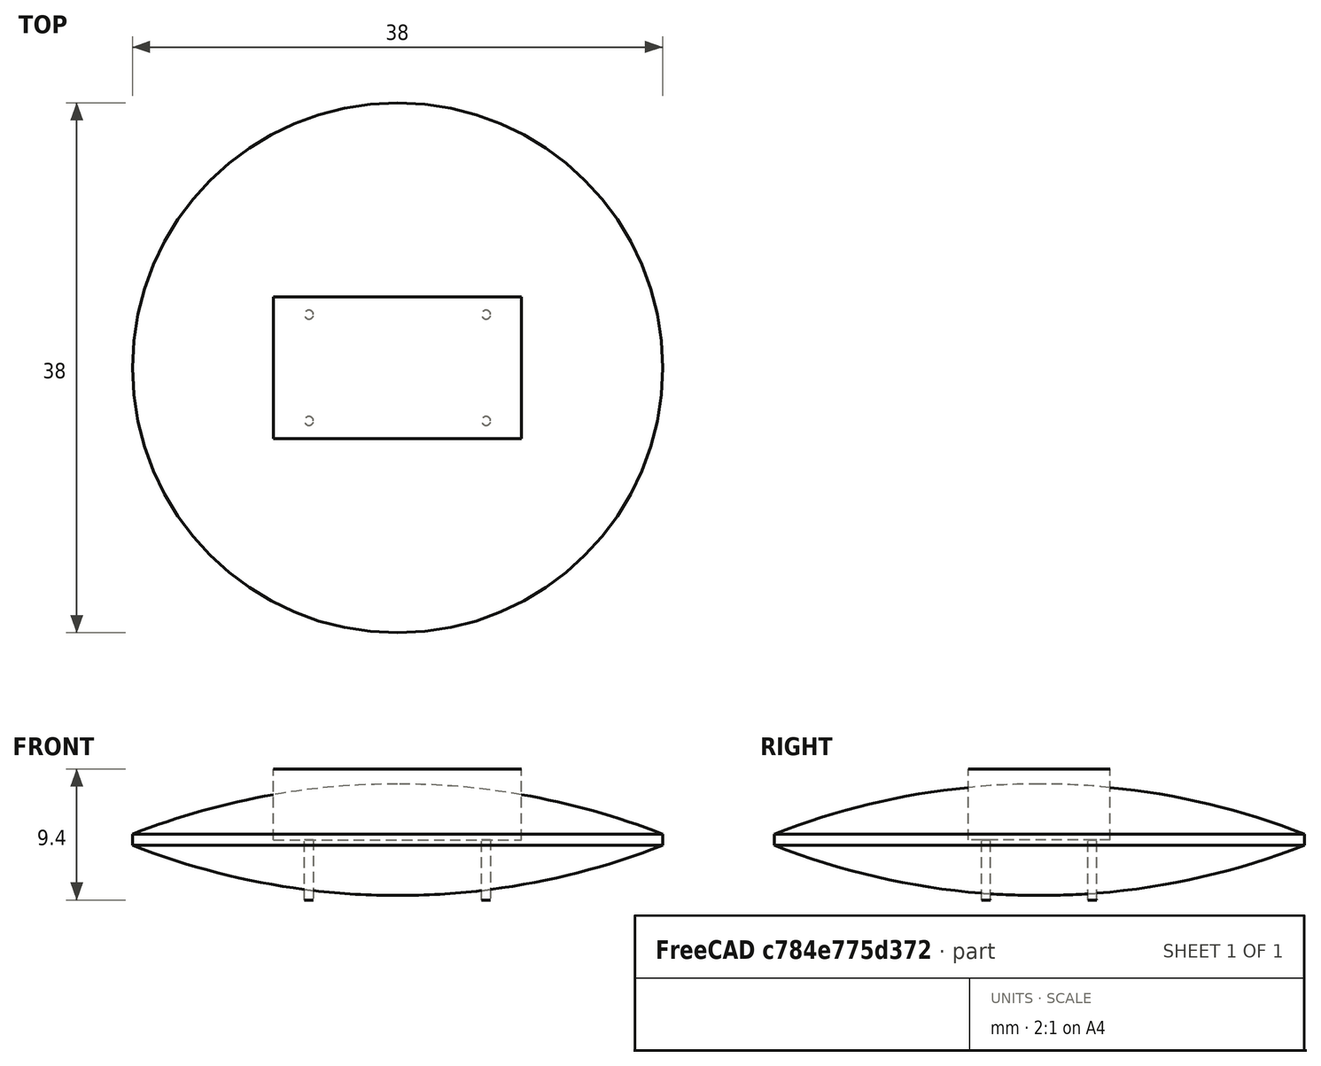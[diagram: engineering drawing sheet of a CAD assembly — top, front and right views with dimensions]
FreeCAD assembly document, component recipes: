
FREECAD ASSEMBLY — COMPONENT RECIPES ("ClockRaytrace")

This assembly document has 4 components, labeled P0..P3 below (a component is one placed body or linked part). 4 of them carry a construction recipe — the FreeCAD feature program that regenerates the part from scratch, quoted from this document or its linked companion documents; the rest are supplied as boundary geometry only. No exploded tour is included for this assembly.
COMPONENT P0 — recipe-attached ("baffle", modeled in this document).
Construction recipe (the document's own serialized feature program — sketch geometry with constraints, then the solid features built on it; lengths are millimeters unless a unit is written):

FEATURE [Sketcher::SketchObject] Sketch011
  ArcFitTolerance = 1e-06
  AttachmentSupport = -> [XY_Plane019]
  FullyConstrained = false
  MakeInternals = false
  MapMode = 5
  sketch-geometry (3):
    g0: Circle CenterX=0 CenterY=0 CenterZ=0 NormalX=0 NormalY=0 NormalZ=1 AngleXU=0 Radius=20
    g1: Circle CenterX=0 CenterY=0 CenterZ=0 NormalX=0 NormalY=0 NormalZ=1 AngleXU=0 Radius=21.5748
    g2: LineSegment [constr] StartX=0.010426 StartY=20 StartZ=0 EndX=0.010426 EndY=21.5748 EndZ=0
  constraints (7):
    c: Coincident(g0,g-1)
    c: Coincident(g1,g0)
    c: Diameter(g0) = 40
    c: PointOnObject(g2,g0)
    c: PointOnObject(g2,g1)
    c: Vertical(g2)
    c: DistanceY(g2,g2) = 1.5748
FEATURE [PartDesign::Pad] Pad006
  Direction = (0,0,1)
  Length = 48
  Length2 = 10
  Profile = -> Sketch011
  ReferenceAxis = -> Sketch011 [N_Axis]
  Refine = true
  Reversed = true
  Suppressed = false
  Type = 0
  expr: Length = Spreadsheet.Base_LensToLED - 3 mm
FEATURE [PartDesign::Body] Body010  label="baffle"
  AllowCompound = false
  Group = -> [Sketch011,Pad006]
  Origin = -> Origin019
  Placement = pos=(-7.46,0,48) rot=(0,-1,0;0.314159rad)
  Tip = -> Pad006
  expr: .Placement.Base.x = 2.54 mm - Spreadsheet.Base_Lens_X_offset
  expr: .Placement.Base.z = Spreadsheet.Base_LensToLED - 3 mm
COMPONENT P1 — recipe-attached ("Wall and Ceiling", modeled in this document).
Construction recipe (the document's own serialized feature program — sketch geometry with constraints, then the solid features built on it; lengths are millimeters unless a unit is written):

FEATURE [Sketcher::SketchObject] Sketch012
  ArcFitTolerance = 1e-06
  AttachmentSupport = -> [XZ_Plane022]
  FullyConstrained = true
  MakeInternals = false
  MapMode = 5
  Placement = pos=(0,0,0) rot=(0,0.707107,0.707107;3.14159rad)
  sketch-geometry (6):
    g0: LineSegment StartX=-76.2 StartY=0 StartZ=0 EndX=-76.2 EndY=1390.42 EndZ=0
    g1: LineSegment StartX=-76.2 StartY=1390.42 StartZ=0 EndX=1751.03 EndY=1390.42 EndZ=0
    g2: LineSegment StartX=1751.03 StartY=1390.42 StartZ=0 EndX=1751.03 EndY=1391.99 EndZ=0
    g3: LineSegment StartX=1751.03 StartY=1391.99 StartZ=0 EndX=-77.7748 EndY=1391.99 EndZ=0
    g4: LineSegment StartX=-77.7748 StartY=1391.99 StartZ=0 EndX=-77.7748 EndY=0 EndZ=0
    g5: LineSegment StartX=-77.7748 StartY=0 StartZ=0 EndX=-76.2 EndY=0 EndZ=0
  constraints (18):
    c: Vertical(g0)
    c: Horizontal(g1)
    c: Coincident(g2,g1)
    c: Vertical(g2)
    c: Horizontal(g3)
    c: PointOnObject(g4,g-1)
    c: Vertical(g4)
    c: Coincident(g5,g0)
    c: DistanceY(g2,g2) = 1.5748
    c: Equal(g5,g2)
    c: Coincident(g3,g2)
    c: Coincident(g3,g4)
    c: Coincident(g1,g0)
    c: Coincident(g5,g4)
    c: DistanceX(g0,g-1) = 76.2
    c: DistanceY(g4,g4) = 1391.99
    c: DistanceX(g3,g3) = 1828.8
    c: Horizontal(g0,g-1)
FEATURE [PartDesign::Pad] Pad007
  Direction = (0,1,-2e-16)
  Length = 1524
  Length2 = 10
  Midplane = true
  Placement = pos=(0,0,0) rot=(1,0,0;1.5708rad)
  Profile = -> Sketch012
  ReferenceAxis = -> Sketch012 [N_Axis]
  Refine = true
  Suppressed = false
  Type = 0
FEATURE [PartDesign::Body] Body011  label="Wall and Ceiling"
  AllowCompound = false
  Group = -> [Sketch012,Pad007]
  Origin = -> Origin020
  Tip = -> Pad007
  expr: .Placement.Rotation.Pitch = Spreadsheet.Base_DeviceTilt
COMPONENT P2 — recipe-attached ("LED001", modeled in this document).
Construction recipe (the document's own serialized feature program — sketch geometry with constraints, then the solid features built on it; lengths are millimeters unless a unit is written):

FEATURE [PartDesign::ShapeBinder] CopyPad004
  TraceSupport = false
FEATURE [Sketcher::SketchObject] Sketch
  ArcFitTolerance = 1e-06
  AttachmentSupport = -> [CopyPad004]
  FullyConstrained = true
  MakeInternals = false
  MapMode = 5
  Placement = pos=(0,0,0) rot=(1,0,0;3.14159rad)
  sketch-geometry (5):
    g0: LineSegment StartX=8.89 StartY=-5.08 StartZ=0 EndX=8.89 EndY=5.08 EndZ=0
    g1: LineSegment StartX=8.89 StartY=5.08 StartZ=0 EndX=-8.89 EndY=5.08 EndZ=0
    g2: LineSegment StartX=-8.89 StartY=5.08 StartZ=0 EndX=-8.89 EndY=-5.08 EndZ=0
    g3: LineSegment StartX=-8.89 StartY=-5.08 StartZ=0 EndX=8.89 EndY=-5.08 EndZ=0
    g4: GeomPoint [constr] X=0 Y=0 Z=0
  constraints (12):
    c: Coincident(g0,g1)
    c: Coincident(g1,g2)
    c: Coincident(g2,g3)
    c: Coincident(g3,g0)
    c: Vertical(g0)
    c: Vertical(g2)
    c: Horizontal(g1)
    c: Horizontal(g3)
    c: Symmetric(g2,g0,g4)
    c: Coincident(g4,g-1)
    c: DistanceY(g0,g0) = 10.16
    c: DistanceX(g1,g1) = 17.78
FEATURE [PartDesign::Pad] Pad
  Direction = (0,0,-1)
  Length = 5.08
  Length2 = 10
  Profile = -> Sketch
  ReferenceAxis = -> Sketch [N_Axis]
  Refine = true
  Reversed = true
  Suppressed = false
  Type = 0
FEATURE [Sketcher::SketchObject] Sketch013
  ArcFitTolerance = 1e-06
  AttachmentSupport = -> [CopyPad004]
  FullyConstrained = true
  MakeInternals = false
  MapMode = 5
  Placement = pos=(0,0,0) rot=(1,0,0;3.14159rad)
  sketch-geometry (9):
    g0: LineSegment [constr] StartX=6.35 StartY=-3.81 StartZ=0 EndX=6.35 EndY=3.81 EndZ=0
    g1: LineSegment [constr] StartX=6.35 StartY=3.81 StartZ=0 EndX=-6.35 EndY=3.81 EndZ=0
    g2: LineSegment [constr] StartX=-6.35 StartY=3.81 StartZ=0 EndX=-6.35 EndY=-3.81 EndZ=0
    g3: LineSegment [constr] StartX=-6.35 StartY=-3.81 StartZ=0 EndX=6.35 EndY=-3.81 EndZ=0
    g4: GeomPoint [constr] X=0 Y=0 Z=0
    g5: Circle CenterX=-6.35 CenterY=-3.81 CenterZ=0 NormalX=0 NormalY=0 NormalZ=1 AngleXU=0 Radius=0.3175
    g6: Circle CenterX=6.35 CenterY=-3.81 CenterZ=0 NormalX=0 NormalY=0 NormalZ=1 AngleXU=0 Radius=0.3175
    g7: Circle CenterX=6.35 CenterY=3.81 CenterZ=0 NormalX=0 NormalY=0 NormalZ=1 AngleXU=0 Radius=0.3175
    g8: Circle CenterX=-6.35 CenterY=3.81 CenterZ=0 NormalX=0 NormalY=0 NormalZ=1 AngleXU=0 Radius=0.3175
  constraints (20):
    c: Coincident(g0,g1)
    c: Coincident(g1,g2)
    c: Coincident(g2,g3)
    c: Coincident(g3,g0)
    c: Vertical(g0)
    c: Vertical(g2)
    c: Horizontal(g1)
    c: Horizontal(g3)
    c: Symmetric(g2,g0,g4)
    c: Coincident(g4,g-1)
    c: DistanceX(g1,g1) = 12.7
    c: DistanceY(g2,g2) = 7.62
    c: Coincident(g5,g2)
    c: Coincident(g6,g0)
    c: Coincident(g7,g0)
    c: Coincident(g8,g1)
    c: Equal(g5,g8)
    c: Equal(g7,g8)
    c: Equal(g6,g8)
    c: Diameter(g8) = 0.635
FEATURE [PartDesign::Pad] Pad008
  BaseFeature = -> Pad
  Direction = (0,0,-1)
  Length = 4.318
  Length2 = 10
  Profile = -> Sketch013
  ReferenceAxis = -> Sketch013 [N_Axis]
  Refine = true
  Suppressed = false
  Type = 0
FEATURE [PartDesign::Body] Body
  AllowCompound = false
  Group = -> [CopyPad004,Sketch,Pad,Sketch013,Pad008]
  Origin = -> Origin
  Tip = -> Pad008
COMPONENT P3 — recipe-attached ("38mm50FLLens001", modeled in this document).
Construction recipe (the document's own serialized feature program — sketch geometry with constraints, then the solid features built on it; lengths are millimeters unless a unit is written):

FEATURE [Sketcher::SketchObject] Sketch001
  ArcFitTolerance = 1e-06
  AttachmentSupport = -> [XZ_Plane003]
  FullyConstrained = true
  MakeInternals = false
  MapMode = 5
  Placement = pos=(0,0,0) rot=(1,0,0;1.5708rad)
  sketch-geometry (7):
    g0: LineSegment StartX=0 StartY=3.99545 StartZ=0 EndX=0 EndY=-3.99545 EndZ=0
    g1: LineSegment [constr] StartX=0 StartY=0 StartZ=0 EndX=19 EndY=0 EndZ=0
    g2: LineSegment StartX=19 StartY=0.4 StartZ=0 EndX=19 EndY=-0.4 EndZ=0
    g3: Circle [constr] CenterX=0 CenterY=-48.0045 CenterZ=0 NormalX=0 NormalY=0 NormalZ=1 AngleXU=0 Radius=52
    g4: ArcOfCircle CenterX=1.31e-14 CenterY=-48.0045 CenterZ=0 NormalX=0 NormalY=0 NormalZ=1 AngleXU=0 Radius=52 StartAngle=1.19675 EndAngle=1.5708
    g5: Circle [constr] CenterX=0 CenterY=48.0045 CenterZ=0 NormalX=0 NormalY=0 NormalZ=1 AngleXU=0 Radius=52
    g6: ArcOfCircle CenterX=4.1e-15 CenterY=48.0045 CenterZ=0 NormalX=0 NormalY=0 NormalZ=1 AngleXU=0 Radius=52 StartAngle=4.71239 EndAngle=5.08643
  constraints (21):
    c: Vertical(g0)
    c: Symmetric(g0,g0,g-1)
    c: Coincident(g1,g-1)
    c: PointOnObject(g1,g-1)
    c: DistanceX(g1,g1) = 19
    c: Vertical(g2)
    c: Symmetric(g2,g2,g1)
    c: Radius(g3) = 52
    c: Vertical(g3,g0)
    c: PointOnObject(g2,g3)
    c: PointOnObject(g0,g3)
    c: Coincident(g4,g0)
    c: Coincident(g4,g2)
    c: Vertical(g5,g0)
    c: Equal(g5,g3)
    c: PointOnObject(g2,g5)
    c: Coincident(g6,g2)
    c: Coincident(g6,g0)
    c: Equal(g4,g3)
    c: Equal(g5,g6)
    c: DistanceY(g2,g2) = 0.8
FEATURE [PartDesign::Revolution] Revolution001
  Angle = 360
  Angle2 = 60
  Axis = (0,2e-16,1)
  Base = (0,0,0)
  Placement = pos=(0,0,0) rot=(1,0,0;1.5708rad)
  Profile = -> Sketch001
  ReferenceAxis = -> Sketch001 [V_Axis]
  Refine = true
  Reversed = true
  Suppressed = false
  Type = 0
FEATURE [PartDesign::Body] Body001  label="38mm50FLLens"
  AllowCompound = false
  Group = -> [Sketch001,Revolution001]
  Origin = -> Origin003
  Tip = -> Revolution001
PROVENANCE & LICENSES
A FreeCAD (.FCStd) document from a public repository crawl; recipes are the document's own serialized feature recipes (and, for linked parts, companion documents' recipes).
License: mit.
